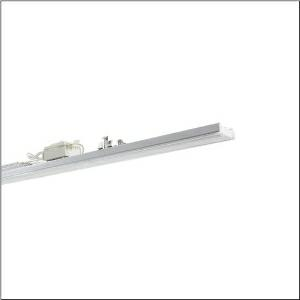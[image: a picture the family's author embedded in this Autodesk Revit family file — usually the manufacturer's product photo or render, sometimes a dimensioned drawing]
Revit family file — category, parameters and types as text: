
# Revit family: licross_r__11_recessed_mo_51te1e7n485g_91bb
name_source: partatom
category: Lighting Fixtures
units: mm (PartAtom-declared; Revit-internal decimal feet)

## family parameters
Cut with Voids When Loaded = No
Host = Face
Light Source = No
Part Type = Normal
Room Calculation Point = No
Round Connector Dimension = Use Diameter
Shared = No

## types (1)
- Licross® 11 Recessed MO (1 x LED, 8660 lm, 48.5 W, 4000K)
    Apparent Load = 49 VA
    CIE Flux Codes = 85 95 99 100 100
    Color Rendering = 80
    Color Temperature = 4000K
    Default Elevation = 1800 mm
    Description = Licross® 11 Recessed MO, luminaire insert, of sheet steel, galvanised, coil coated, white, length: 1.500mm, width: 66mm, height: 67mm, LED rated luminous flux: 8.660lm, light colour: 840, control gear: ON/OFF, with plug, 3-pole, with phase selection, mains connection: 220..240V, AC, 50/60Hz, rated input power: 49W, halogen-free wiring, primary light control with lens, of plastic, primary optical cover: cover, of PMMA, light emission: direct distribution, primary light characteristic: symmetric, protection rating (complete): IP54, insulation class (complete): insulation class I (protective earthing), certification: CE, ENEC, VDE, UKCA, protection symbol: D if used in an environment with non-conductive dust loads with corresponding accessories, impact resistance: IK06, permissible ambient temperature for indoor applications: -35..+35°C, corresponds to IFS (International Featured Standards) requirements for safety and quality in the food industry, reducing of maximum allowable ambient temperature of 5°C with ceiling mounting, packaging unit: 1 piece
    Height = 58 mm
    Lamp = 1 x LED
    Lamp Light Flux = 8660 lm
    Lamp Power = 48.5 W
    Lamp count = 1
    Length = 1500 mm
    Luminous efficacy = 179 lm/W
    Manufacturer = Siteco
    ModVariant = No
    Model = 51TE1E7N485G
    Mounting Place = Ceiling
    Mounting Type = Pendant
    Number of Poles = 1
    OnlyDefault = Yes
    Power Factor = 1
    Product Name = Licross® 11 Recessed MO
    Product group = luminaire insert
    ProductGroupID = 902
    Protection Class = Protection class I
    Protection Degree = IP 54
    RLX_Detail_Level = 1
    RLX_Emergency_Light_Flux = 0 lm
    RLX_Emergency_Type = 0
    RLX_Emergency_Type_DB = No
    RlxData = <blob elided: 20881 chars, md5=02447ae2>
    Socket = socket
    Standby Power = 0 W
    System Light Flux = 8660 lm
    System Power = 49 W
    Type Comments = Product without accessories
    Type Image = l_1296930.jpg
    URL = http://relux.com
    VarID = ---
    Voltage = 0 V
    Weight = 0.00 kg
    Width = 66 mm

## geometry (parser evidence)
native form markers: Blend x4, Sweep x12
no freeform markers — native parametric forms only
